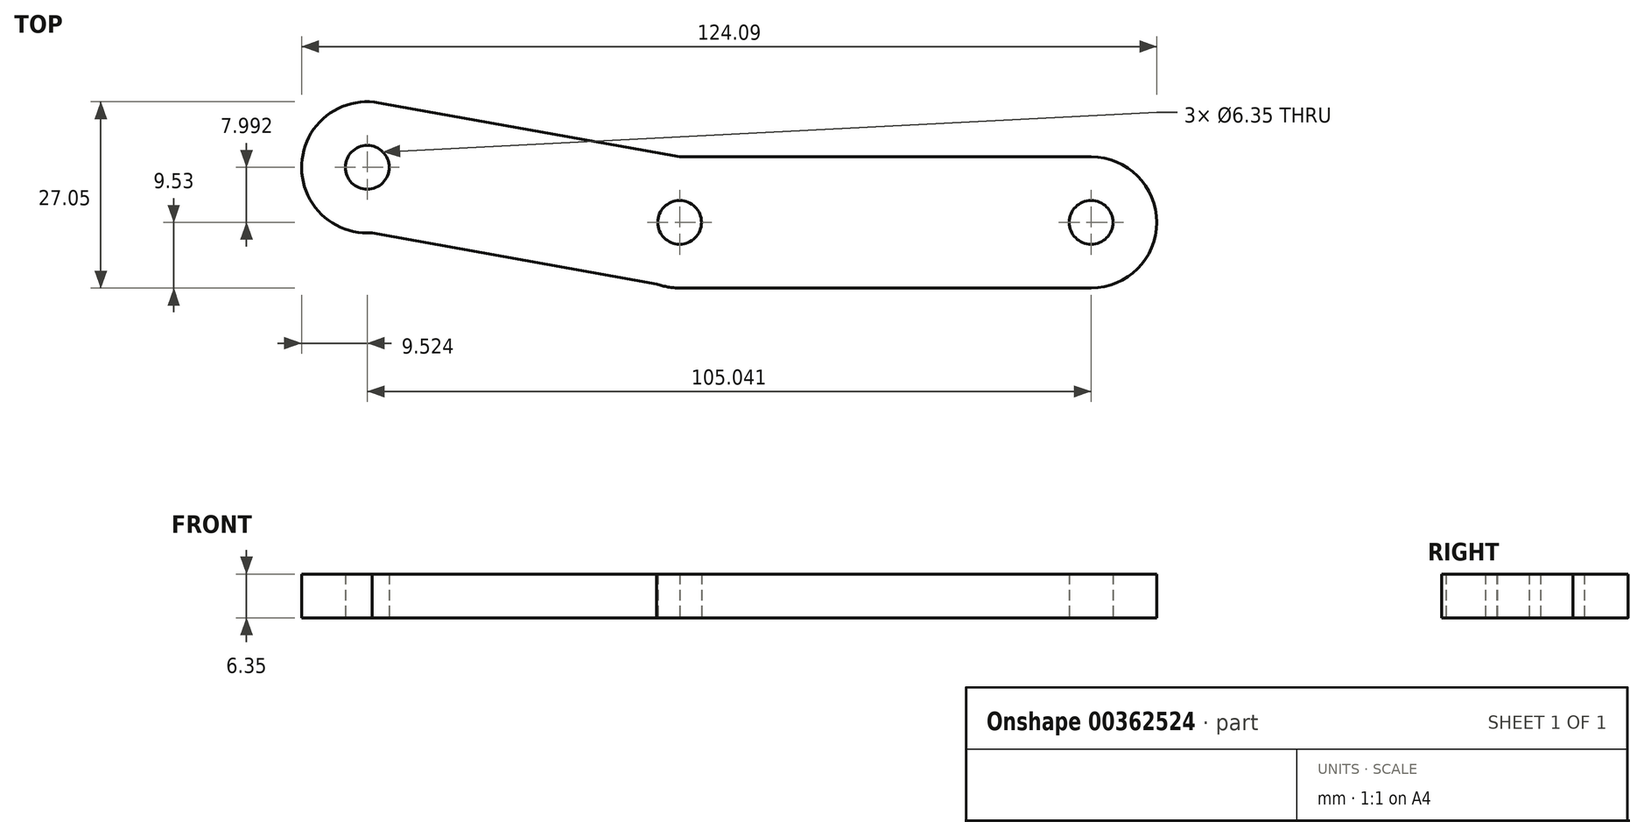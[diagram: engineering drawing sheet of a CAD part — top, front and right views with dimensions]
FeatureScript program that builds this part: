
annotation { "Feature Type Name" : "Feature", "Feature Type Description" : "" }
export const myFeature = defineFeature(function(context is Context, id is Id, definition is map)
    precondition{}
    {
        {
            var Q0;
            Q0=qCreatedBy(makeId("Top.planeOp"),FACE);
            var sketch = newSketch(context, id + "F0", { "sketchPlane" : qUnion([Q0])});
            skLineSegment(sketch, "E0", {"start": v(0, 0) * mm, "end": v(59.72, 0) * mm});
            skLineSegment(sketch, "E1", {"start": v(0, 0) * mm, "end": v(-46.02, 0) * mm});
            skLineSegment(sketch, "E2", {"start": v(0, 0) * mm, "end": v(-45.33, 8) * mm});
            skCircle(sketch, "E3", {"center": v(0, 0) * mm, "radius": 3.18 * mm});
            skCircle(sketch, "E4", {"center": v(59.72, 0) * mm, "radius": 3.18 * mm});
            skCircle(sketch, "E5", {"center": v(0, 0) * mm, "radius": 9.53 * mm});
            skCircle(sketch, "E6", {"center": v(59.72, 0) * mm, "radius": 9.53 * mm});
            skCircle(sketch, "E7", {"center": v(-45.33, 8) * mm, "radius": 3.18 * mm});
            skCircle(sketch, "E8", {"center": v(-45.33, 8) * mm, "radius": 9.53 * mm});
            skLineSegment(sketch, "E9", {"start": v(0, -9.53) * mm, "end": v(59.72, -9.53) * mm});
            skLineSegment(sketch, "E10", {"start": v(59.72, 9.53) * mm, "end": v(0, 9.53) * mm});
            skLineSegment(sketch, "E11", {"start": v(0, 9.52) * mm, "end": v(-43.64, 17.37) * mm});
            skLineSegment(sketch, "E12", {"start": v(0, -9.53) * mm, "end": v(-49.3, -0.67) * mm});
            skSolve(sketch);
        }
        {
            var Q0;
            Q0 = qSketchRegion(id + "F0", true);
            var Q1;
            {var subQ0=sQuery(id+"F0.wireOp",EDGE,"E8");var subQ1=sQuery(id+"F0.wireOp",EDGE,"E1");var subQ2=makeQuery(id+"F0.imprint","INTERSECT",VERTEX,{"derivedFrom":[subQ1,subQ0]});Q1=makeQuery(id+"F0.imprint","IMPRINT",FACE,{"disambiguationData":[TD([[makeQuery(id+"F0.imprint","IMPRINT",EDGE,{"disambiguationData":[TD([[subQ2,1.0]])],"derivedFrom":subQ1}),-1.0]])]});}
            var Q2;
            {var subQ0=sQuery(id+"F0.wireOp",EDGE,"E3");var subQ1=sQuery(id+"F0.wireOp",EDGE,"E1");var subQ2=makeQuery(id+"F0.imprint","INTERSECT",VERTEX,{"derivedFrom":[subQ1,subQ0]});Q2=makeQuery(id+"F0.imprint","IMPRINT",FACE,{"disambiguationData":[TD([[makeQuery(id+"F0.imprint","IMPRINT",EDGE,{"disambiguationData":[TD([[subQ2,-1.0]])],"derivedFrom":subQ1}),-1.0]])]});}
            extrude(context, id + "F1", {"entities" : qUnion([Q0, Q1, Q2]), "depth" : 6.35 * mm});
        }
    });
